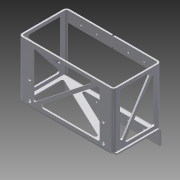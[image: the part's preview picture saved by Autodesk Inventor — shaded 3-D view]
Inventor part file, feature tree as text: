
AUTODESK INVENTOR PART (.ipt)
format: ipt  version: 2015 SP1 (Build 190203100, 203)  size: 451,072 bytes
history: native  units: in
note: dims shown in document units (in); Inventor stores cm internally (conversion verified against a paired STEP export)
features: other x29, sheet_metal_op x12, sketch x6, projected_geometry x5, hole x3
ambient origin geometry x8: Origin, YZ Plane, XZ Plane, XY Plane, X Axis, Y Axis, Z Axis, Center Point
bodies: Solid1 (feature_tree)
feature tree (55):
  other  "<userpath>\Documents\2015 Offseason Chassis\West Coast Chassis Fall 2015\rivet(rv).xlsx"
  other  "front"
  other  "back_supporting"
  other  "back_mounting"
  other  "left_side"
  other  "right_side"
  other  "right_back"
  other  "left_back"
  hole  "bottom_rivet_holes"  [1 undecoded]
  other  "top_rivet_sketch"
  hole  "compressor_mounting_holes"  [1 undecoded]
  hole  "top_rivet_holes"  [1 undecoded]
  other  "front_sketch"
  other  "Plate1"
  sketch  "Sketch2"  dims[d0=7.1in d1=4.376in]
  other  "Plate2"
  sheet_metal_op  "Bend1"
  sheet_metal_op  "Corner1"
  sketch  "Sketch3"  dims[d2=0.12in d3=0.12in]
  other  "Plate3"
  sheet_metal_op  "Bend2"
  sheet_metal_op  "Corner2"
  sketch  "Sketch4"  dims[d4=0.06in d5=0.24in]
  other  "Plate4"
  sheet_metal_op  "Bend3"
  sheet_metal_op  "Corner3"
  sketch  "Sketch5"  dims[d6=0.12in]
  other  "Plate5"
  sheet_metal_op  "Bend4"
  sheet_metal_op  "Corner4"
  sketch  "Sketch8"  dims[d7=3.45in]
  other  "Plate8"
  sheet_metal_op  "Bend7"
  sheet_metal_op  "Corner7"
  sketch  "Sketch9"  dims[d8=90.0deg d9=0.12in d10=0.48in d11=0.12in d12=0.12in d13=0.12in d14=0.06in d15=0.24in d16=0.12in d17=1.0in d18=90.0deg d19=0.12in d20=0.48in d21=0.12in d22=0.12in d23=0.12in d24=0.06in d25=0.24in d26=0.12in d27=3.45in d28=90.0deg d29=0.12in d30=0.48in d31=0.12in d32=0.12in d33=0.12in d34=0.06in d35=0.24in d36=0.12in d37=3.45in d38=90.0deg d39=0.12in d40=0.48in d41=0.12in d42=0.12in d63=0.12in d64=0.06in d65=0.24in d66=0.12in d67=3.49in d68=90.0deg d69=0.12in d70=0.48in d71=0.12in d72=0.12in d73=0.12in d74=0.06in d75=0.24in d76=0.12in d77=3.49in d78=90.0deg d79=0.12in d80=0.48in d81=0.12in d82=0.12in d83=0.1406in d84=0.75in d85=0.375in d86=0.25in d87=0.5635in d88=0.12in d89=0.8108in d105=0.25in d106=1.42in d108=5.51in d109=0.25in d110=0.75in d111=0.375in d112=0.25in d113=0.5635in d114=0.12in d115=0.8108in d116=0.5in d117=0.1406in d118=0.75in d119=0.375in d120=0.25in d121=0.5635in d122=0.12in d123=0.8108in d124=0.25in d125=0.25in d126=0.25in d127=0.25in d128=0.25in d129=0.25in d130=0.25in d131=0.125in d132=0.12in d133=0.0in d134=0.25in d135=0.12in d136=0.0in d137=0.25in d138=0.25in d139=0.25in d140=0.25in d141=0.25in d142=0.25in d143=0.25in d144=0.125in d145=0.12in d146=0.0in d147=0.25in d148=0.25in d149=0.25in d150=0.25in d151=0.25in d152=0.25in d153=0.25in d154=0.125in d155=0.12in d156=0.0in d157=0.5in d158=0.25in d159=0.25in d160=0.25in d161=0.25in d162=0.25in d163=0.125in d164=0.12in d165=0.0in d166=0.5in]
  other  "Plate9"
  sheet_metal_op  "Bend8"
  sheet_metal_op  "Corner8"
  other  "bottom_rivet_sketch"
  projected_geometry  "Projected Loop1"
  other  "cmp_mountings_sketch"
  projected_geometry  "Projected Loop4"
  other  "front_speed_sketch"
  other  "back_speed_hole_sketch"
  other  "left_speed_sketch"
  projected_geometry  "Projected Loop5"
  other  "right_speed_sketch"
  projected_geometry  "Projected Loop6"
  other  "bottom_speed_sketch"
  projected_geometry  "Projected Loop7"
  other  "front_speed_cut"
  other  "back_speed_cut"
  other  "left_speed_cut"
  other  "right_speed_cut"
  other  "bottom_speed_cut"
note: 3 required parameter values undecoded (feature->parameter linkage not recoverable at this tier; creation-order binding heuristic only, values carry confidence <= 0.55)
